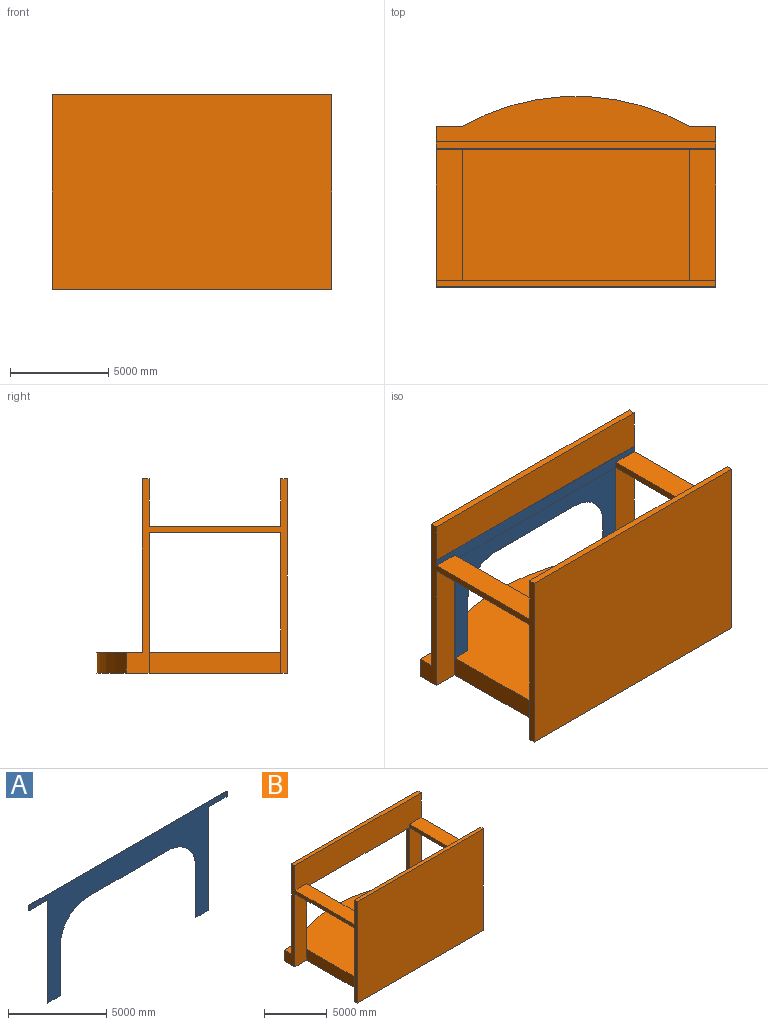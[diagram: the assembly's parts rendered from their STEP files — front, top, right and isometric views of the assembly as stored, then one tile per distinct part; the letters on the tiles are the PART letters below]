
ASSEMBLY  parts=2 mates=1
PART A: 16 faces, bbox 14249.4x19.1x6756.4 mm
  f0: plane 6426.2x19.05mm, normal (1,0,0), area 122419.1mm2, adj f1,f13,f14,f15
  f1: plane 1333.5x19.05mm, normal (0,0,-1), area 25403.2mm2, adj f0,f2,f14,f15
  f2: plane 330.2x19.05mm, normal (1,0,0), area 6290.3mm2, adj f1,f3,f14,f15
  f3: plane 14249.4x19.05mm, normal (0,0,1), area 271451.1mm2, adj f2,f4,f14,f15
  f4: plane 330.2x19.05mm, normal (-1,0,0), area 6290.3mm2, adj f3,f5,f14,f15
  f5: plane 1333.5x19.05mm, normal (0,0,-1), area 25403.2mm2, adj f4,f6,f14,f15
  f6: plane 6426.2x19.05mm, normal (-1,0,0), area 122419.1mm2, adj f5,f7,f14,f15
  f7: plane 914.4x19.05mm, normal (0,0,-1), area 17419.3mm2, adj f6,f8,f14,f15
  f8: plane 3149.6x19.05mm, normal (1,0,0), area 59999.9mm2, adj f7,f9,f14,f15
  f9: cylinder r=2032mm len=2032mm, axis (0,1,0), area 60804.9mm2, adj f8,f10,f14,f15
  f10: plane 5689.6x19.05mm, normal (0,0,-1), area 108386.9mm2, adj f9,f11,f14,f15
  f11: cylinder r=2032mm len=2032mm, axis (0,1,0), area 60804.9mm2, adj f10,f12,f14,f15
  f12: plane 3149.6x19.05mm, normal (-1,0,0), area 59999.9mm2, adj f11,f13,f14,f15
  f13: plane 914.4x19.05mm, normal (0,0,-1), area 17419.3mm2, adj f0,f12,f14,f15
  f14: plane 14249.4x6756.4mm, normal (0,-1,0), area 30368909.3mm2, adj f0,f1,f2,f3,f4,f5,f6,f7
  f15: plane 14249.4x6756.4mm, normal (0,1,0), area 30368909.3mm2, adj f0,f1,f2,f3,f4,f5,f6,f7
PART B: 26 faces, bbox 14249.4x9734.6x9906 mm
  f0: plane 7162.8x1333.5mm, normal (0,-1,0), area 9551593.8mm2, adj f4,f6,f11,f15,f24
  f1: plane 14249.4x9906mm, normal (0,1,0), area 127917808.7mm2, adj f3,f4,f5,f6,f10,f11,f19,f20
  f2: plane 14249.4x2743.2mm, normal (0,-1,0), area 38208310.7mm2, adj f6,f10,f16,f17,f20,f22,f23,f25
  f3: plane 14249.4x9404.35mm, normal (0,0,1), area 105409688.2mm2, adj f1,f4,f5,f6,f7,f8,f9,f10
  f4: plane 6718.3x1066.8mm, normal (1,0,0), area 7167082.4mm2, adj f0,f1,f3,f11
  f5: plane 6718.3x1066.8mm, normal (-1,0,0), area 7167082.4mm2, adj f1,f3,f11,f12
  f6: plane 9906x8216.9mm, normal (1,0,0), area 9822883.6mm2, adj f0,f1,f2,f3,f7,f11,f14,f17
  f7: plane 1333.5x1066.8mm, normal (0,1,0), area 1422577.8mm2, adj f3,f6,f8,f11
  f8: cylinder r=11808.14mm len=11582.4mm, axis (0,0,1), area 12914267.8mm2, adj f3,f7,f9,f11
  f9: plane 1333.5x1066.8mm, normal (0,1,0), area 1422577.8mm2, adj f3,f8,f10,f11
  f10: plane 9906x8216.9mm, normal (-1,0,0), area 9822883.6mm2, adj f1,f2,f3,f9,f11,f12,f14,f17
  f11: plane 14249.4x9734.55mm, normal (0,0,-1), area 111046289.8mm2, adj f0,f1,f4,f5,f6,f7,f8,f9
  f12: plane 7162.8x1333.5mm, normal (0,-1,0), area 9551593.8mm2, adj f5,f10,f11,f13,f21
  f13: plane 6096x349.25mm, normal (1,0,0), area 2129028mm2, adj f3,f12,f14,f16
  f14: plane 14249.4x8839.2mm, normal (0,1,0), area 55346986.1mm2, adj f3,f6,f10,f13,f15,f16,f17
  f15: plane 6096x349.25mm, normal (-1,0,0), area 2129028mm2, adj f0,f3,f14,f16
  f16: plane 11582.4x349.25mm, normal (0,0,-1), area 4045153.2mm2, adj f2,f13,f14,f15
  f17: plane 14249.4x349.25mm, normal (0,0,1), area 4976603mm2, adj f2,f6,f10,f14
  f18: plane 14249.4x9906mm, normal (0,-1,0), area 141154556.4mm2, adj f6,f10,f11,f19
  f19: plane 14249.4x330.2mm, normal (0,0,1), area 4705151.9mm2, adj f1,f6,f10,f18
  f20: plane 6718.3x330.2mm, normal (1,0,0), area 2218382.7mm2, adj f1,f2,f21,f22
  f21: plane 6718.3x1333.5mm, normal (0,0,-1), area 8958853mm2, adj f1,f10,f12,f20
  f22: plane 6718.3x1333.5mm, normal (0,0,1), area 8958853mm2, adj f1,f2,f10,f20
  f23: plane 6718.3x330.2mm, normal (-1,0,0), area 2218382.7mm2, adj f1,f2,f24,f25
  f24: plane 6718.3x1333.5mm, normal (0,0,-1), area 8958853mm2, adj f0,f1,f6,f23
  f25: plane 6718.3x1333.5mm, normal (0,0,1), area 8958853mm2, adj f1,f2,f6,f23
PLACE A t=(3788.93,1122.54,6442.15)mm
PLACE B t=(3788.93,-2061.98,3394.15)mm
MATE fastened A.f1 <-> B.f25  axis (0,0,1) through (9580.13,1122.54,9820.35)mm
